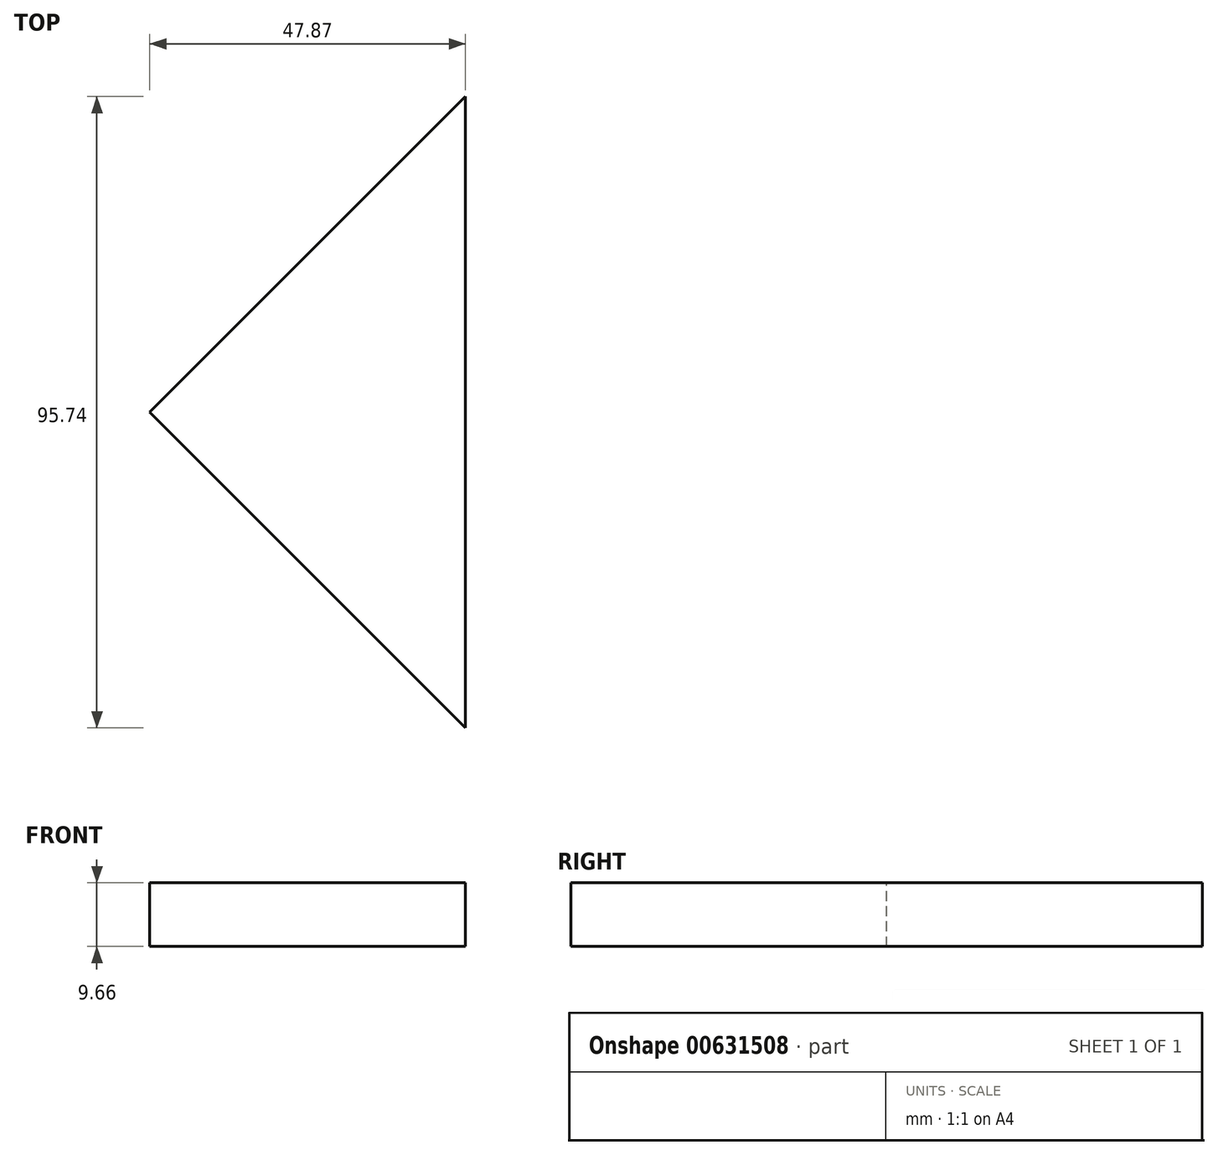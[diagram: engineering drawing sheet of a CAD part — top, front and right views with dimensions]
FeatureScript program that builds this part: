
annotation { "Feature Type Name" : "Feature", "Feature Type Description" : "" }
export const myFeature = defineFeature(function(context is Context, id is Id, definition is map)
    precondition{}
    {
        {
            var Q0;
            Q0=qCreatedBy(makeId("Front.planeOp"),FACE);
            var sketch = newSketch(context, id + "F0", { "sketchPlane" : qUnion([Q0])});
            skLineSegment(sketch, "E0", {"start": v(-25.34, -5.45) * mm, "end": v(-12.99, -5.45) * mm});
            skLineSegment(sketch, "E1", {"start": v(26.13, -5.45) * mm, "end": v(26.13, 4.01) * mm});
            skLineSegment(sketch, "E2", {"start": v(26.13, 4.01) * mm, "end": v(21.4, 4.01) * mm});
            skLineSegment(sketch, "E3", {"start": v(-25.45, 4.01) * mm, "end": v(-25.34, -5.45) * mm});
            skLineSegment(sketch, "E4", {"start": v(-12.99, -5.45) * mm, "end": v(-10.95, 4.01) * mm});
            skLineSegment(sketch, "E5", {"start": v(12.41, -5.45) * mm, "end": v(110.31, 97.6) * mm});
            skLineSegment(sketch, "E6", {"start": v(110.31, 97.6) * mm, "end": v(64.41, 119.36) * mm});
            skLineSegment(sketch, "E7", {"start": v(-12.99, -5.45) * mm, "end": v(12.41, -5.45) * mm});
            skLineSegment(sketch, "E8", {"start": v(12.41, -5.45) * mm, "end": v(26.13, -5.45) * mm});
            skLineSegment(sketch, "E9", {"start": v(64.41, 119.36) * mm, "end": v(18.51, 141.13) * mm});
            skLineSegment(sketch, "E10", {"start": v(-10.95, 4.01) * mm, "end": v(18.51, 141.13) * mm});
            skLineSegment(sketch, "E11", {"start": v(-10.95, 4.01) * mm, "end": v(-25.45, 4.01) * mm});
            skLineSegment(sketch, "E12", {"start": v(28.17, 49.44) * mm, "end": v(-0.29, -5.45) * mm});
            skSolve(sketch);
        }
        {
            var Q0;
            Q0=sQuery(id+"F0.wireOp",EDGE,"E10");
            var Q1;
            Q1=sQuery(id+"F0.wireOp",EDGE,"E12");
            revolve(context, id + "F1", {"bodyType" : ToolBodyType.SURFACE, "surfaceEntities" : qUnion([Q0]), "axis" : qUnion([Q1]), "revolveType" : RevolveType.FULL});
        }
        {
            var Q0;
            Q0=qCreatedBy(makeId("Top.planeOp"),FACE);
            var sketch = newSketch(context, id + "F2", { "sketchPlane" : qUnion([Q0])});
            skLineSegment(sketch, "E13", {"start": v(-49.2, 0) * mm, "end": v(-128.84, 0) * mm});
            skLineSegment(sketch, "E14", {"start": v(-23.5, 0) * mm, "end": v(24.38, 47.87) * mm});
            skLineSegment(sketch, "E15.MirrorCS", {"start": v(-23.5, 0) * mm, "end": v(24.38, -47.87) * mm});
            skLineSegment(sketch, "E16", {"start": v(24.38, 47.87) * mm, "end": v(24.38, -47.87) * mm});
            skSolve(sketch);
        }
        {
            var Q0;
            Q0 = qSketchRegion(id + "F2", true);
            extrude(context, id + "F3", {"entities" : qUnion([Q0]), "endBound" : BoundingType.SYMMETRIC, "oppositeDirection" : true, "depth" : 9.65 * mm, "offsetDistance" : 25.4 * mm});
        }
    });
